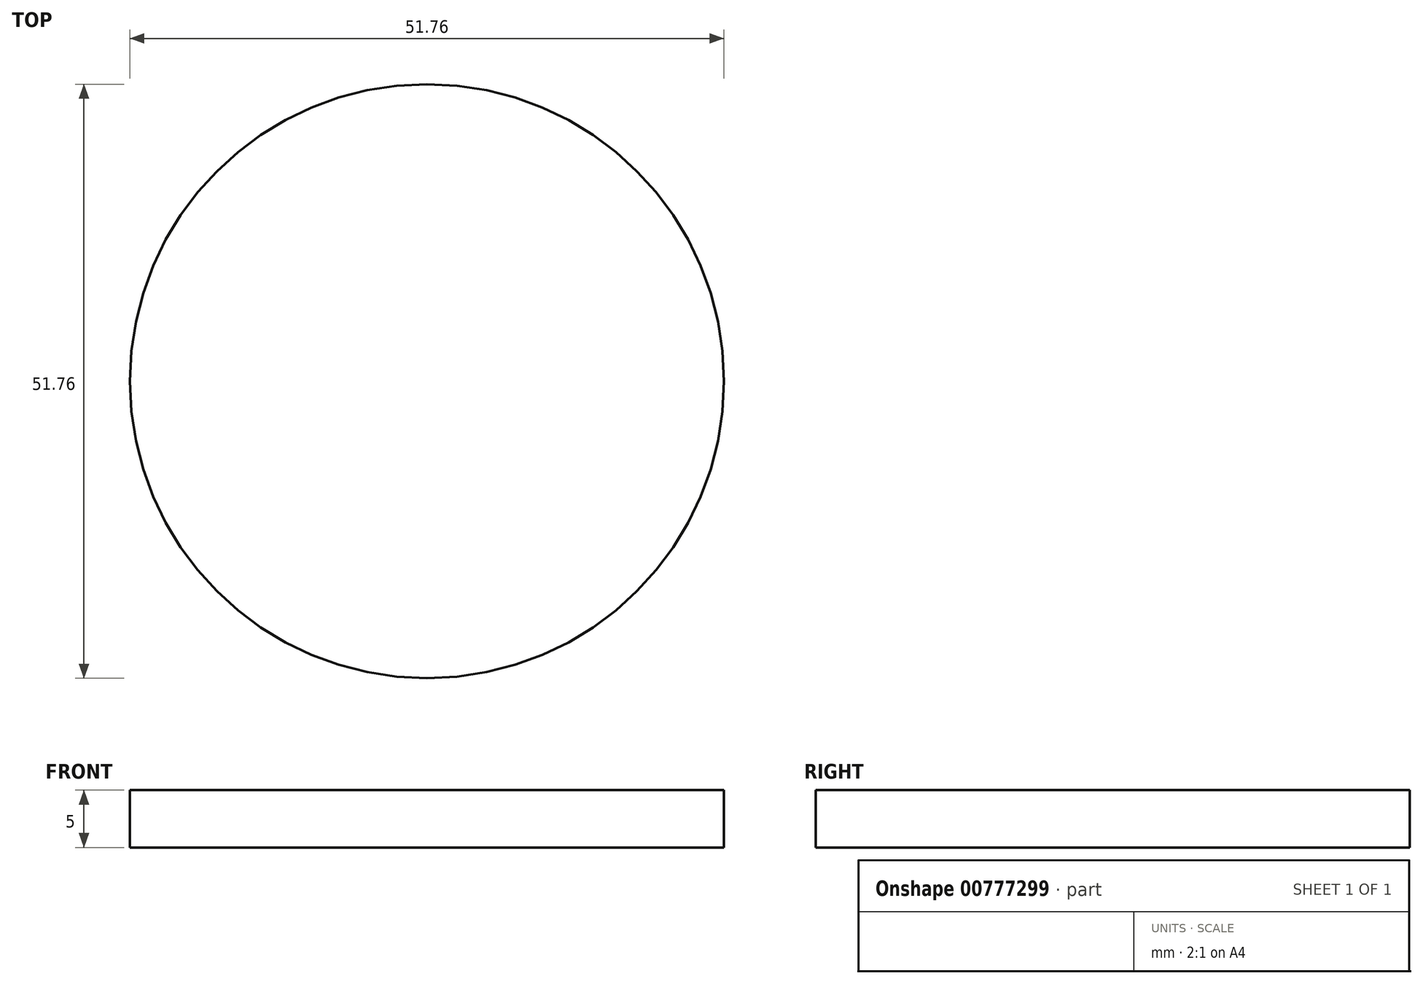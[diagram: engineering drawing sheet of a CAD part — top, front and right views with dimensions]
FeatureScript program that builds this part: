
annotation { "Feature Type Name" : "Feature", "Feature Type Description" : "" }
export const myFeature = defineFeature(function(context is Context, id is Id, definition is map)
    precondition{}
    {
        {
            var Q0;
            Q0=qCreatedBy(makeId("Top.planeOp"),FACE);
            var sketch = newSketch(context, id + "F0", { "sketchPlane" : qUnion([Q0])});
            skCircle(sketch, "E0", {"center": v(0, 0) * mm, "radius": 25.88 * mm});
            skSolve(sketch);
        }
        {
            var Q0;
            Q0=sQuery(id+"F0.wireOp",EDGE,"E0");
            extrude(context, id + "F1", {"bodyType" : ToolBodyType.SURFACE, "surfaceEntities" : qUnion([Q0]), "depth" : 5 * mm, "offsetDistance" : 25.4 * mm});
        }
    });
